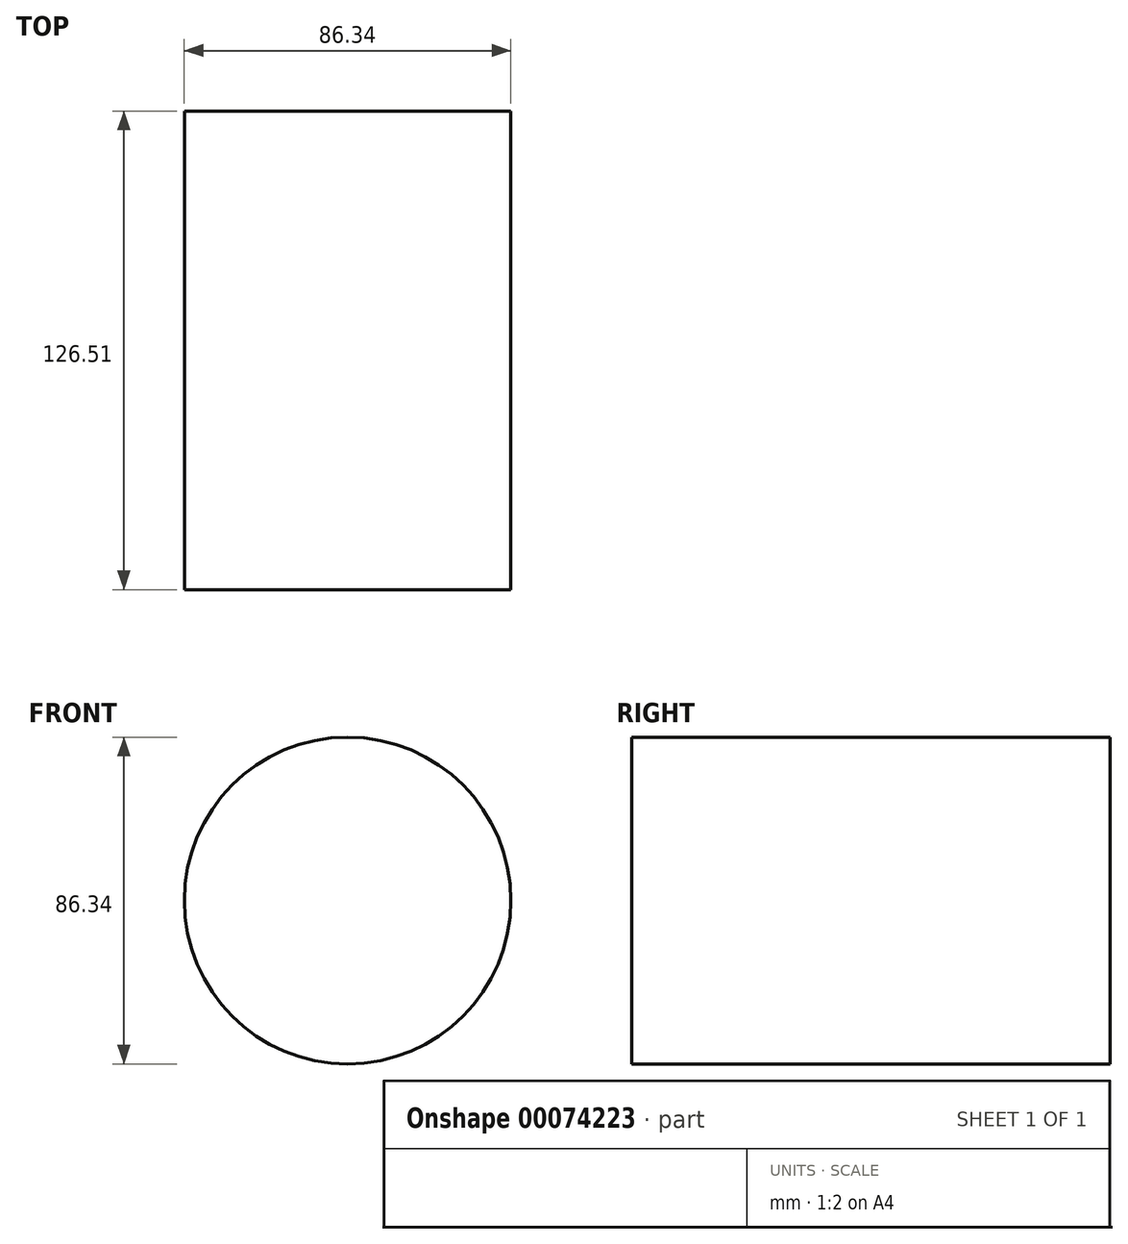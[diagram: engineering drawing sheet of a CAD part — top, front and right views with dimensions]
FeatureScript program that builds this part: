
annotation { "Feature Type Name" : "Feature", "Feature Type Description" : "" }
export const myFeature = defineFeature(function(context is Context, id is Id, definition is map)
    precondition{}
    {
        {
            var Q0;
            Q0=qCreatedBy(makeId("Front.planeOp"),FACE);
            var sketch = newSketch(context, id + "F0", { "sketchPlane" : qUnion([Q0])});
            skCircle(sketch, "E0", {"center": v(-35.43, 18.85) * mm, "radius": 43.17 * mm});
            skSolve(sketch);
        }
        {
            var Q0;
            Q0 = qSketchRegion(id + "F0", true);
            extrude(context, id + "F1", {"entities" : qUnion([Q0]), "depth" : 126.5 * mm});
        }
    });
